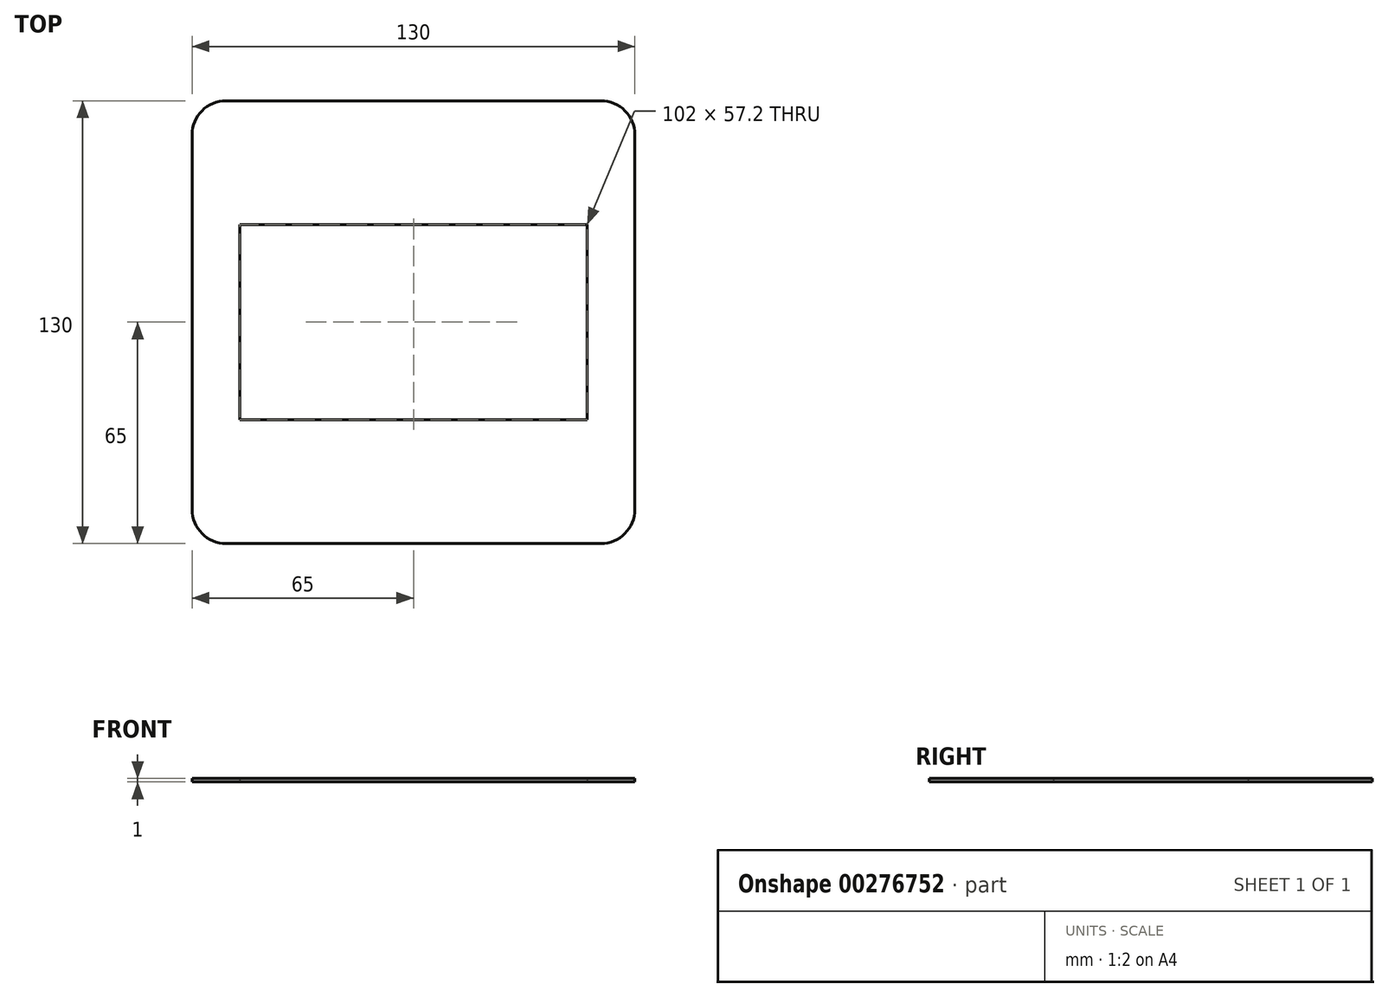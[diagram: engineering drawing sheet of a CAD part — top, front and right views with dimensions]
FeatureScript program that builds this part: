
annotation { "Feature Type Name" : "Feature", "Feature Type Description" : "" }
export const myFeature = defineFeature(function(context is Context, id is Id, definition is map)
    precondition{}
    {
        {
            var Q0;
            Q0=qCreatedBy(makeId("Top.planeOp"),FACE);
            var sketch = newSketch(context, id + "F0", { "sketchPlane" : qUnion([Q0])});
            skLineSegment(sketch, "E0.bottom", {"start": v(-10, 0) * mm, "end": v(-120, 0) * mm});
            skLineSegment(sketch, "E0.top", {"start": v(-10, -130) * mm, "end": v(-120, -130) * mm});
            skLineSegment(sketch, "E0.left", {"start": v(0, -10) * mm, "end": v(0, -120) * mm});
            skLineSegment(sketch, "E0.right", {"start": v(-130, -10) * mm, "end": v(-130, -120) * mm});
            skPoint(sketch, "E1.visualSharp", {"position": v(-130, 0) * mm});
            skArc(sketch, "E1.filletArc", {"start": v(-120, 0) * mm, "mid": v(-127.07, -2.93) * mm, "end": v(-130, -10) * mm});
            skPoint(sketch, "E2.visualSharp", {"position": v(0, 0) * mm});
            skArc(sketch, "E2.filletArc", {"start": v(0, -10) * mm, "mid": v(-2.93, -2.93) * mm, "end": v(-10, 0) * mm});
            skPoint(sketch, "E3.visualSharp", {"position": v(0, -130) * mm});
            skArc(sketch, "E3.filletArc", {"start": v(-10, -130) * mm, "mid": v(-2.93, -127.07) * mm, "end": v(0, -120) * mm});
            skPoint(sketch, "E4.visualSharp", {"position": v(-130, -130) * mm});
            skArc(sketch, "E4.filletArc", {"start": v(-130, -120) * mm, "mid": v(-127.07, -127.07) * mm, "end": v(-120, -130) * mm});
            skLineSegment(sketch, "E5.bottom", {"start": v(-116, -36.4) * mm, "end": v(-14, -36.4) * mm});
            skLineSegment(sketch, "E5.top", {"start": v(-116, -93.6) * mm, "end": v(-14, -93.6) * mm});
            skLineSegment(sketch, "E5.left", {"start": v(-116, -36.4) * mm, "end": v(-116, -93.6) * mm});
            skLineSegment(sketch, "E5.right", {"start": v(-14, -36.4) * mm, "end": v(-14, -93.6) * mm});
            skSolve(sketch);
        }
        {
            var Q0;
            Q0 = qSketchRegion(id + "F0", true);
            extrude(context, id + "F1", {"entities" : qUnion([Q0]), "depth" : 1 * mm});
        }
    });
